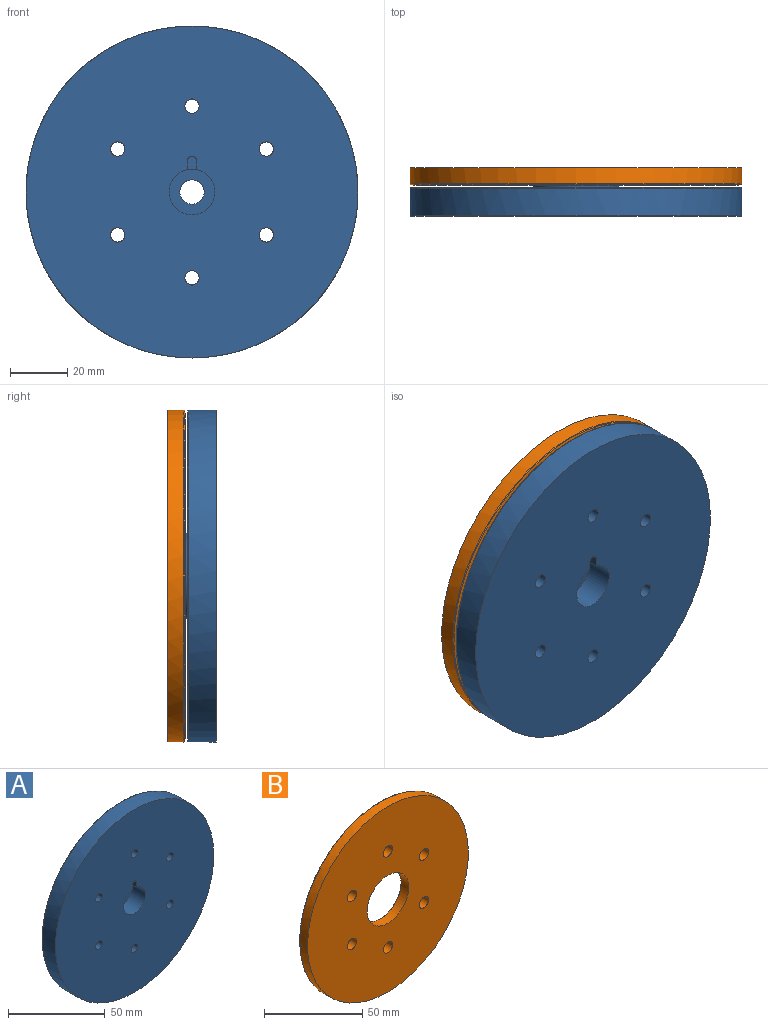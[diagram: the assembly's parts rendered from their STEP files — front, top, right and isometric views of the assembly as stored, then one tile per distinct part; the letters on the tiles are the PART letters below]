
ASSEMBLY  parts=2 mates=1
PART A: 22 faces, bbox 130x16.8x130 mm
  f0: cylinder r=2.5mm len=10mm, axis (0,-1,0), area 157.1mm2, adj f5,f8
  f1: cylinder r=2.5mm len=10mm, axis (0,-1,0), area 157.1mm2, adj f5,f8
  f2: cylinder r=2.5mm len=10mm, axis (0,-1,0), area 157.1mm2, adj f5,f8
  f3: cylinder r=2.5mm len=10mm, axis (0,-1,0), area 157.1mm2, adj f5,f8
  f4: cylinder r=2.5mm len=10mm, axis (0,-1,0), area 157.1mm2, adj f5,f8
  f5: plane 116x116mm, normal (0,-1,0), area 10236.8mm2, adj f0,f1,f2,f3,f4,f6,f7,f15
  f6: cylinder r=8mm len=16mm, axis (0,-1,0), area 477mm2, adj f5,f14,f15,f17,f18
  f7: cylinder r=58mm len=116mm, axis (0,-1,0), area 3478.2mm2, adj f5,f10
  f8: plane 113x113mm, normal (0,1,0), area 9204.1mm2, adj f0,f1,f2,f3,f4,f9,f11,f19
  f9: torus R=56.5mm, axis (0,-1,0), area 463.5mm2, adj f8,f10
  f10: torus R=57.7mm, axis (0,1,0), area 143.3mm2, adj f7,f9
  f11: cylinder r=15mm len=30mm, axis (0,-1,0), area 593.8mm2, adj f8,f21
  f12: plane 29x29mm, normal (0,1,0), area 589.6mm2, adj f20,f21
  f13: cylinder r=4.25mm len=8.5mm, axis (0,-1,0), area 168.2mm2, adj f14,f20
  f14: plane 16x16mm, normal (0,-1,0), area 144.3mm2, adj f6,f13
  f15: plane 8.5x3.14mm, normal (-1,0,0), area 26.7mm2, adj f5,f6,f16,f18
  f16: cylinder r=1.5mm len=8.5mm, axis (0,-1,0), area 40.1mm2, adj f5,f15,f17,f18
  f17: plane 8.5x3.14mm, normal (1,0,0), area 26.7mm2, adj f5,f6,f16,f18
  f18: plane 4.64x3mm, normal (0,-1,0), area 12.7mm2, adj f6,f15,f16,f17
  f19: cylinder r=2.5mm len=10mm, axis (0,-1,0), area 157.1mm2, adj f5,f8
  f20: cone r=4.75mm half-angle=45deg, axis (0,1,0), area 20mm2, adj f12,f13
  f21: cone r=14.5mm half-angle=45deg, axis (0,-1,0), area 65.5mm2, adj f11,f12
PART B: 13 faces, bbox 130x6x130 mm
  f0: cylinder r=3.3mm len=6.6mm, axis (0,-1,0), area 124.4mm2, adj f8,f11
  f1: cylinder r=3.3mm len=6.6mm, axis (0,-1,0), area 124.4mm2, adj f8,f11
  f2: cylinder r=3.3mm len=6.6mm, axis (0,-1,0), area 124.4mm2, adj f8,f11
  f3: cylinder r=3.3mm len=6.6mm, axis (0,-1,0), area 124.4mm2, adj f8,f11
  f4: cylinder r=3.3mm len=6.6mm, axis (0,-1,0), area 124.4mm2, adj f8,f11
  f5: cylinder r=58mm len=116mm, axis (0,-1,0), area 2020.5mm2, adj f10,f11
  f6: cylinder r=15mm len=30mm, axis (0,-1,0), area 518.4mm2, adj f11,f12
  f7: cylinder r=3.3mm len=6.6mm, axis (0,-1,0), area 124.4mm2, adj f8,f11
  f8: plane 113x113mm, normal (0,1,0), area 9068.7mm2, adj f0,f1,f2,f3,f4,f7,f9,f12
  f9: torus R=56.5mm, axis (0,-1,0), area 463.5mm2, adj f8,f10
  f10: torus R=57.7mm, axis (0,1,0), area 143.3mm2, adj f5,f9
  f11: plane 116x116mm, normal (0,-1,0), area 9656.2mm2, adj f0,f1,f2,f3,f4,f5,f6,f7
  f12: cone r=15.5mm half-angle=45deg, axis (0,1,0), area 67.8mm2, adj f6,f8
PLACE A t=(-90.31,90.28,-34.87)mm
PLACE B rot(axis=(-1,0,0),180deg) t=(-90.31,111.08,-34.87)mm
MATE parallel A.f19 <-> B.f7  axis (0,1,0) through (-90.31,100.28,-4.87)mm
